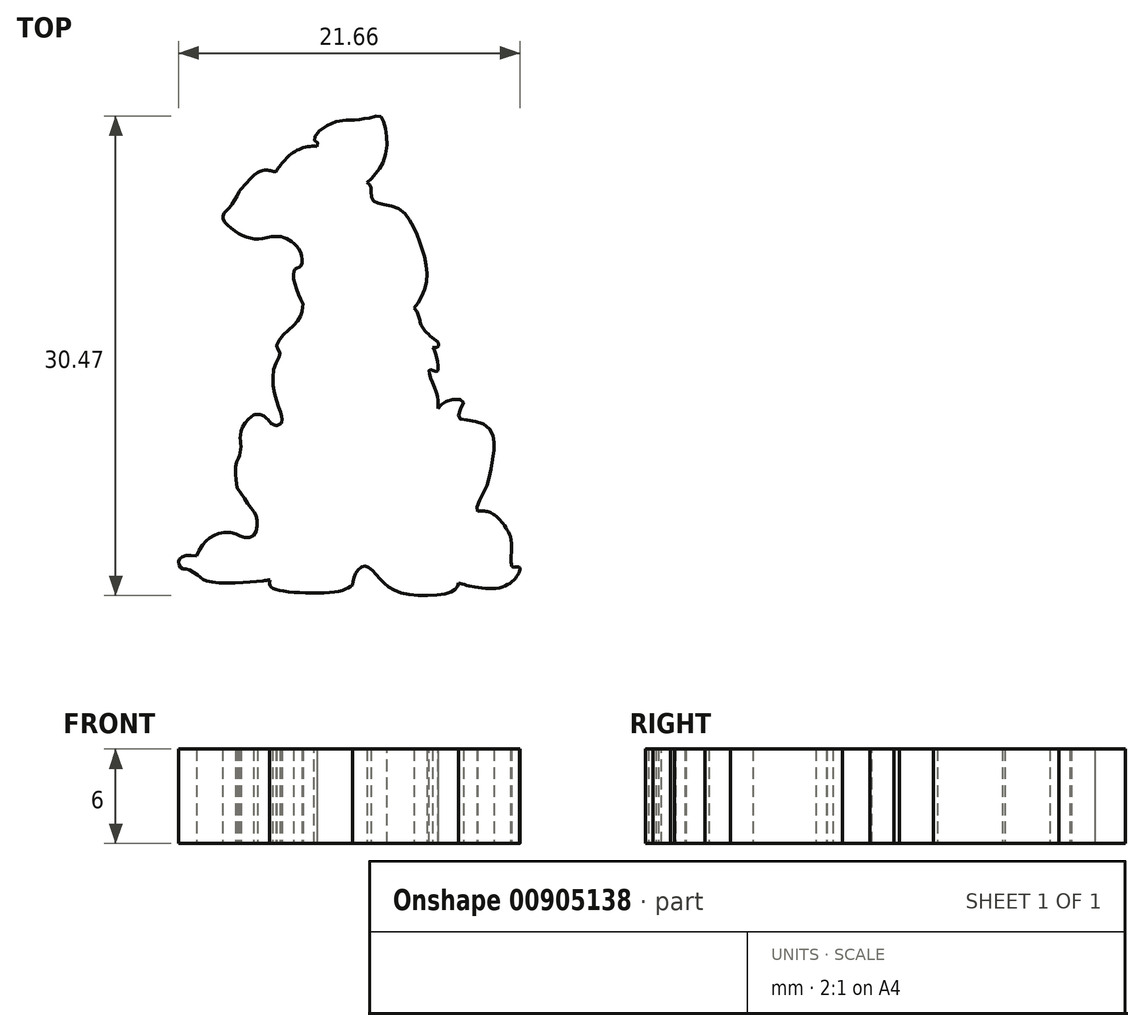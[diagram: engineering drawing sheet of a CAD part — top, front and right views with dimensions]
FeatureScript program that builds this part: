
annotation { "Feature Type Name" : "Feature", "Feature Type Description" : "" }
export const myFeature = defineFeature(function(context is Context, id is Id, definition is map)
    precondition{}
    {
        {
            var Q0;
            Q0=qCreatedBy(makeId("Top.planeOp"),FACE);
            var sketch = newSketch(context, id + "F0", { "sketchPlane" : qUnion([Q0])});
            skFitSpline(sketch, "E0", {"points": [v(-5.14, 11.66) * mm, v(-4.15, 12.8) * mm, v(-2.53, 13.27) * mm], "startDerivative": vector(1.57, 2.44) * mm, "endDerivative": vector(3.63, -0.34) * mm});
            skFitSpline(sketch, "E1", {"points": [v(-5.14, 11.66) * mm, v(-6, 11.74) * mm, v(-7.48, 10.4) * mm], "startDerivative": vector(-1.75, -0.04) * mm, "endDerivative": vector(-2.35, -2.77) * mm});
            skFitSpline(sketch, "E2", {"points": [v(-7.48, 10.4) * mm, v(-8.14, 9.34) * mm, v(-8.53, 8.78) * mm, v(-8, 8.07) * mm, v(-7.01, 7.5) * mm, v(-6.05, 7.4) * mm, v(-4.82, 7.53) * mm], "startDerivative": vector(-3.21, -6.45) * mm, "endDerivative": vector(6.79, -1.36) * mm});
            skFitSpline(sketch, "E3", {"points": [v(-4.82, 7.53) * mm, v(-4.18, 7.24) * mm, v(-3.58, 6.53) * mm, v(-3.58, 5.65) * mm, v(-3.97, 5.43) * mm, v(-3.7, 3.81) * mm, v(-2.39, 2.15) * mm, v(-0.6, 1.29) * mm], "startDerivative": vector(5.85, -2) * mm, "endDerivative": vector(8.31, -1.32) * mm});
            skFitSpline(sketch, "E4", {"points": [v(-0.6, 1.29) * mm, v(0, 1.37) * mm, v(1.86, 1.59) * mm, v(3.25, 2.56) * mm, v(3.93, 3.4) * mm, v(4.44, 4.76) * mm, v(4.21, 6.5) * mm, v(3.7, 7.9) * mm, v(2.8, 9.22) * mm, v(1.5, 9.63) * mm, v(0.96, 9.9) * mm, v(0.9, 10.52) * mm, v(0.83, 10.78) * mm, v(0.65, 10.97) * mm], "startDerivative": vector(17.89, 1.74) * mm, "endDerivative": vector(-4.76, 3.16) * mm});
            skFitSpline(sketch, "E5", {"points": [v(-2.53, 13.27) * mm, v(-2.52, 13.52) * mm, v(-2.7, 13.64) * mm, v(-2.6, 14.01) * mm, v(-1.36, 14.82) * mm, v(0, 14.95) * mm, v(0.34, 15) * mm, v(0.92, 15.1) * mm, v(1.48, 15.17) * mm, v(1.76, 14.57) * mm, v(1.91, 13.39) * mm, v(1.58, 12.07) * mm, v(1.13, 11.47) * mm, v(0.65, 10.97) * mm], "startDerivative": vector(1.9, 6.96) * mm, "endDerivative": vector(-5.83, -4.24) * mm});
            skPoint(sketch, "E6", {"position": v(0, 15) * mm});
            skFitSpline(sketch, "E7", {"points": [v(-3.41, 3.27) * mm, v(-3.48, 2.91) * mm, v(-3.73, 2.21) * mm, v(-4.58, 1.41) * mm, v(-5.1, 0.51) * mm, v(-4.9, 0.15) * mm, v(-5.23, -0.7) * mm, v(-5.23, -2.4) * mm, v(-4.88, -3.55) * mm, v(-4.75, -3.98) * mm, v(-4.78, -4.28) * mm, v(-5.03, -4.45) * mm, v(-5.4, -4.35) * mm, v(-5.93, -3.85) * mm, v(-6.58, -3.8) * mm], "startDerivative": vector(-1.06, -6.28) * mm, "endDerivative": vector(-10, -2.59) * mm});
            skFitSpline(sketch, "E8", {"points": [v(-6.58, -3.8) * mm, v(-7.4, -5.14) * mm, v(-7.38, -5.74) * mm, v(-7.48, -6.45) * mm, v(-7.66, -6.8) * mm, v(-7.7, -7.5) * mm, v(-7.57, -8.47) * mm], "startDerivative": vector(-8, -5.35) * mm, "endDerivative": vector(1.37, 0.2) * mm});
            skFitSpline(sketch, "E9", {"points": [v(-7.57, -8.47) * mm, v(-7.06, -9.24) * mm, v(-6.6, -9.87) * mm, v(-6.4, -10.25) * mm, v(-6.35, -11.05) * mm, v(-6.64, -11.5) * mm, v(-7.23, -11.55) * mm, v(-7.74, -11.32) * mm, v(-8.66, -11.3) * mm, v(-9.24, -11.55) * mm, v(-9.72, -11.92) * mm, v(-10.18, -12.77) * mm], "startDerivative": vector(4.72, -7.44) * mm, "endDerivative": vector(-2.93, -8.91) * mm});
            skFitSpline(sketch, "E10", {"points": [v(-10.18, -12.77) * mm, v(-11.15, -12.83) * mm, v(-11.32, -13.17) * mm, v(-11.13, -13.53) * mm, v(-10.74, -13.6) * mm, v(-10.02, -14.05) * mm, v(-9.51, -14.36) * mm, v(-7.16, -14.44) * mm, v(-5.52, -14.27) * mm], "startDerivative": vector(-8.94, 1.52) * mm, "endDerivative": vector(8.37, 1.14) * mm});
            skFitSpline(sketch, "E11", {"points": [v(-5.52, -14.27) * mm, v(-5.52, -14.64) * mm, v(-4.51, -15) * mm, v(-1.2, -15) * mm, v(-0.27, -14.6) * mm], "startDerivative": vector(-0.66, -2.92) * mm, "endDerivative": vector(3.16, 2.02) * mm});
            skFitSpline(sketch, "E12", {"points": [v(-0.27, -14.6) * mm, v(-0.1, -13.89) * mm, v(0.5, -13.4) * mm, v(1.33, -14.07) * mm, v(2.84, -15.1) * mm, v(6.05, -15) * mm, v(6.46, -14.48) * mm], "startDerivative": vector(0.67, 5.63) * mm, "endDerivative": vector(1.62, 4.8) * mm});
            skFitSpline(sketch, "E13", {"points": [v(6.46, -14.48) * mm, v(7.22, -14.67) * mm, v(8.94, -14.79) * mm, v(9.96, -14.28) * mm, v(10.34, -13.7) * mm], "startDerivative": vector(3.07, -0.88) * mm, "endDerivative": vector(1.45, 3) * mm});
            skFitSpline(sketch, "E14", {"points": [v(10.34, -13.7) * mm, v(10.27, -13.44) * mm, v(9.9, -13.45) * mm, v(9.75, -11.52) * mm], "startDerivative": vector(0.2, 2) * mm, "endDerivative": vector(-0.81, 5) * mm});
            skFitSpline(sketch, "E15", {"points": [v(9.75, -11.52) * mm, v(9.13, -10.53) * mm, v(8.68, -10.1) * mm, v(8.23, -9.92) * mm, v(7.64, -9.92) * mm], "startDerivative": vector(-1.16, 3.02) * mm, "endDerivative": vector(-2.7, -0.23) * mm});
            skFitSpline(sketch, "E16", {"points": [v(7.64, -9.92) * mm, v(7.64, -9.55) * mm, v(8.12, -8.58) * mm, v(8.43, -7.65) * mm, v(8.68, -6.15) * mm, v(8.68, -5.23) * mm, v(8.23, -4.5) * mm, v(7.12, -4.13) * mm, v(6.5, -4.01) * mm, v(6.53, -3.54) * mm, v(6.75, -2.9) * mm, v(6.02, -2.82) * mm, v(5.48, -3.04) * mm, v(5.15, -3.37) * mm], "startDerivative": vector(-1.14, 6.16) * mm, "endDerivative": vector(-5.4, -6.02) * mm});
            skFitSpline(sketch, "E17", {"points": [v(3.64, 3) * mm, v(3.93, 2.44) * mm, v(4.15, 1.77) * mm, v(5.15, 0.85) * mm], "startDerivative": vector(1.6, -1.4) * mm, "endDerivative": vector(3.1, -2.3) * mm});
            skFitSpline(sketch, "E18", {"points": [v(5.15, 0.85) * mm, v(5.15, 0.54) * mm, v(4.79, 0.5) * mm], "startDerivative": vector(0.17, -0.77) * mm, "endDerivative": vector(-0.9, 0.05) * mm});
            skFitSpline(sketch, "E19", {"points": [v(4.79, 0.5) * mm, v(4.94, 0.28) * mm, v(5.15, -0.78) * mm, v(5.04, -1.03) * mm, v(4.61, -0.93) * mm, v(4.94, -2.13) * mm, v(5.14, -2.8) * mm, v(5.15, -3.37) * mm], "startDerivative": vector(1.66, -1.56) * mm, "endDerivative": vector(-0.12, -4.33) * mm});
            skFitSpline(sketch, "E20", {"points": [v(-0.35, -5.1) * mm, v(-0.82, -6.26) * mm, v(-1.02, -7.62) * mm, v(-1.02, -8.87) * mm, v(-1.07, -10.42) * mm, v(-0.85, -12.23) * mm, v(0.23, -11.25) * mm, v(1.24, -11.66) * mm, v(1.6, -12.57) * mm, v(1.8, -12.45) * mm, v(1.91, -11.7) * mm, v(1.92, -9.84) * mm, v(2, -8.8) * mm, v(1.67, -7.37) * mm, v(1.29, -6.14) * mm, v(0.83, -5.3) * mm, v(0.65, -5.21) * mm, v(0.4, -5.77) * mm, v(0, -5.64) * mm, v(-0.35, -5.1) * mm]});
            skFitSpline(sketch, "E21", {"points": [v(-4.78, -4.28) * mm, v(-4.53, -4.6) * mm, v(-4.93, -5.65) * mm, v(-4.78, -6.55) * mm, v(-4.78, -7.7) * mm, v(-5.38, -10.15) * mm, v(-5.38, -10.65) * mm, v(-5.13, -10.8) * mm, v(-5.33, -11.45) * mm, v(-5.93, -12.45) * mm, v(-6, -14.34) * mm], "startDerivative": vector(5.7, -4.05) * mm, "endDerivative": vector(1, -14.85) * mm});
            skFitSpline(sketch, "E22", {"points": [v(5.15, -3.37) * mm, v(4.98, -3.73) * mm, v(4.63, -4.7) * mm, v(4.55, -6.33) * mm, v(5.15, -7.6) * mm, v(5.97, -8.74) * mm, v(6.05, -9.84) * mm, v(6.25, -11.06) * mm, v(6.75, -12.13) * mm, v(6.75, -12.98) * mm, v(6.53, -13.18) * mm, v(6.75, -13.6) * mm, v(6.68, -14.54) * mm], "startDerivative": vector(-2.88, -5.93) * mm, "endDerivative": vector(-2.97, -12.12) * mm});
            skSolve(sketch);
        }
        {
            var Q0;
            Q0=makeQuery(id+"F0.imprint","IMPRINT",FACE,{"disambiguationData":[TD([[makeQuery(id+"F0.imprint","IMPRINT",EDGE,{"derivedFrom":sQuery(id+"F0.wireOp",EDGE,"E0")}),-1.0]])]});
            var Q1;
            {var subQ2=sQuery(id+"F0.wireOp",EDGE,"E11");Q1=makeQuery(id+"F0.imprint","IMPRINT",FACE,{"disambiguationData":[TD([[makeQuery(id+"F0.imprint","IMPRINT",EDGE,{"derivedFrom":subQ2}),1.0]])]});}
            var Q2;
            {var subQ4=sQuery(id+"F0.wireOp",EDGE,"E8");Q2=makeQuery(id+"F0.imprint","IMPRINT",FACE,{"disambiguationData":[TD([[makeQuery(id+"F0.imprint","IMPRINT",EDGE,{"derivedFrom":subQ4}),1.0]])]});}
            var Q3;
            Q3=makeQuery(id+"F0.imprint","IMPRINT",FACE,{"disambiguationData":[TD([[makeQuery(id+"F0.imprint","IMPRINT",EDGE,{"derivedFrom":sQuery(id+"F0.wireOp",EDGE,"E20")}),1.0]])]});
            var Q4;
            {var subQ1=sQuery(id+"F0.wireOp",EDGE,"E14");Q4=makeQuery(id+"F0.imprint","IMPRINT",FACE,{"disambiguationData":[TD([[makeQuery(id+"F0.imprint","IMPRINT",EDGE,{"derivedFrom":subQ1}),1.0]])]});}
            extrude(context, id + "F1", {"entities" : qUnion([Q0, Q1, Q2, Q3, Q4]), "depth" : 6 * mm, "offsetDistance" : 25 * mm});
        }
    });
